# Revit family: Toilet_Elongated-American_Standard-Retrospect_Champion-212AA.104
name_source: partatom
category: Plumbing Fixtures
revit_build: Autodesk Revit 2014 (Build: 20130308_1515(x64)
units: mm (PartAtom-declared; Revit-internal decimal feet)

## types (1)
- 212AA.104
    ADA Compliant = Yes
    Assembly Code = D2010110
    Bowl Shape = Elongated
    CW Connection = Yes
    CWFU = 5
    Cold Water Connection Diameter = 1/2"
    Cold Water Connection Height = 10"
    Cold Water Connection Radius = 1/4"
    Cold Water Connection Width = 6"
    Default Elevation = 16 1/2"
    Description = Retrospect Champion Pro Right Height Elongated Toilet
    Flush Rate = 1.07 gpf / 4.8 Lpf
    HW Connection = No
    HWFU = 0
    Height = 30"
    Installation Type = Floor Mounted
    Length = 30 1/4"
    Manufacturer = American Standard
    Material = Vitreous China-American Standard-020-White
    Model = 212AA.104
    Price = Prices may vary. Please consult Manufacturer Representative for most up-to-date price list.
    Product Documentation Link = https://www.americanstandard-us.com
    Product Page URL = https://www.americanstandard-us.com
    Revised Date = 02/22/2017
    URL = http://www.americanstandard-us.com
    Vent Connection = No
    Visible = Yes
    WFU = 5
    Warranty Information = 10 Year Warranty
    Waste Connection = Yes
    Waste Connection Diameter = 2 3/8"
    Waste Connection Radius = 1 3/16"
    Width = 19 3/4"

## geometry (parser evidence)
native form markers: Sweep x2
no freeform markers — native parametric forms only
